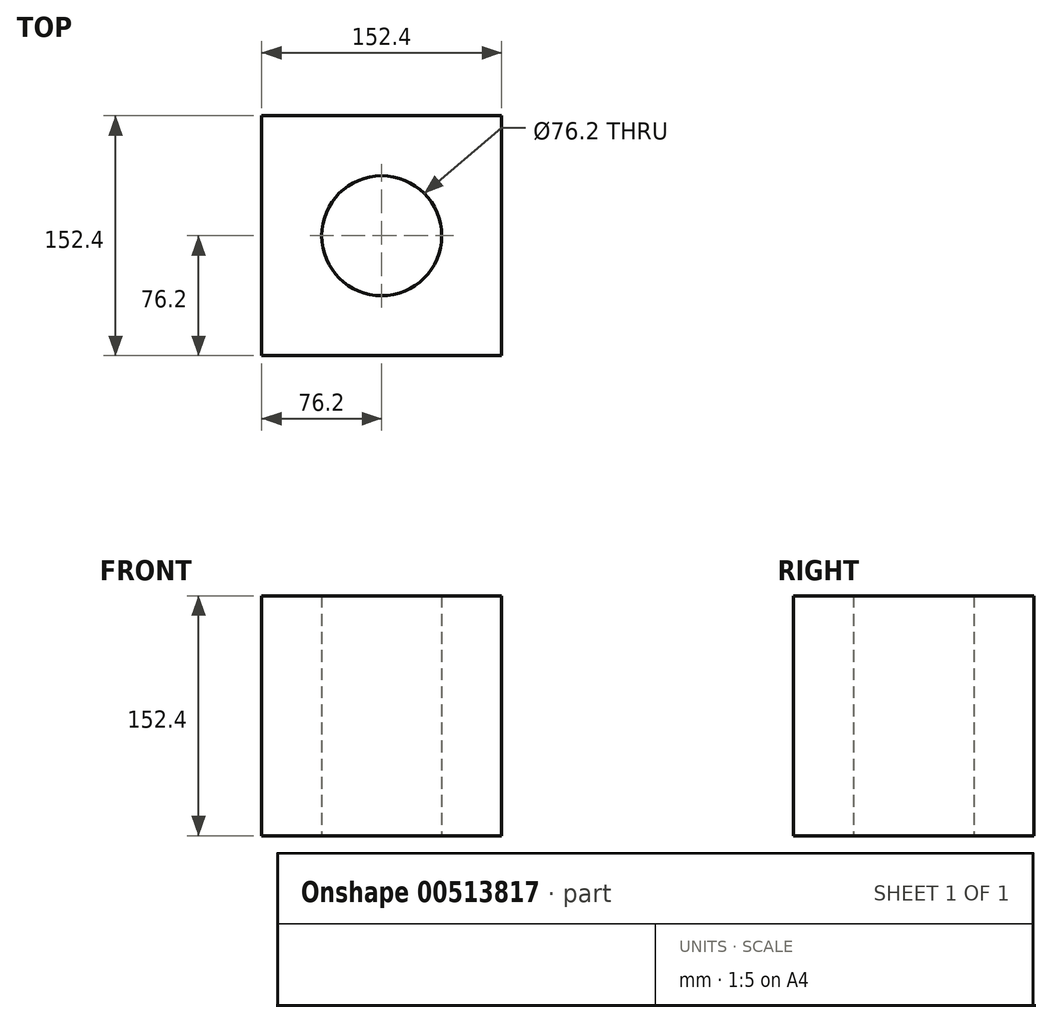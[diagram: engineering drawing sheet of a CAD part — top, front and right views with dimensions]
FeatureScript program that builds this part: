
annotation { "Feature Type Name" : "Feature", "Feature Type Description" : "" }
export const myFeature = defineFeature(function(context is Context, id is Id, definition is map)
    precondition{}
    {
        {
            var Q0;
            Q0=qCreatedBy(makeId("Top.planeOp"),FACE);
            var sketch = newSketch(context, id + "F0", { "sketchPlane" : qUnion([Q0])});
            skLineSegment(sketch, "E0.bottom", {"start": v(76.2, 76.2) * mm, "end": v(-76.2, 76.2) * mm});
            skLineSegment(sketch, "E0.top", {"start": v(76.2, -76.2) * mm, "end": v(-76.2, -76.2) * mm});
            skLineSegment(sketch, "E0.left", {"start": v(76.2, 76.2) * mm, "end": v(76.2, -76.2) * mm});
            skPoint(sketch, "E0.middle", {"position": v(0, 0) * mm});
            skLineSegment(sketch, "E1", {"start": v(-76.2, 76.2) * mm, "end": v(-76.2, -76.2) * mm});
            skCircle(sketch, "E2", {"center": v(0, 0) * mm, "radius": 38.1 * mm});
            skSolve(sketch);
        }
        {
            var Q0;
            Q0 = qSketchRegion(id + "F0", true);
            extrude(context, id + "F1", {"entities" : qUnion([Q0]), "depth" : 152.4 * mm});
        }
    });
